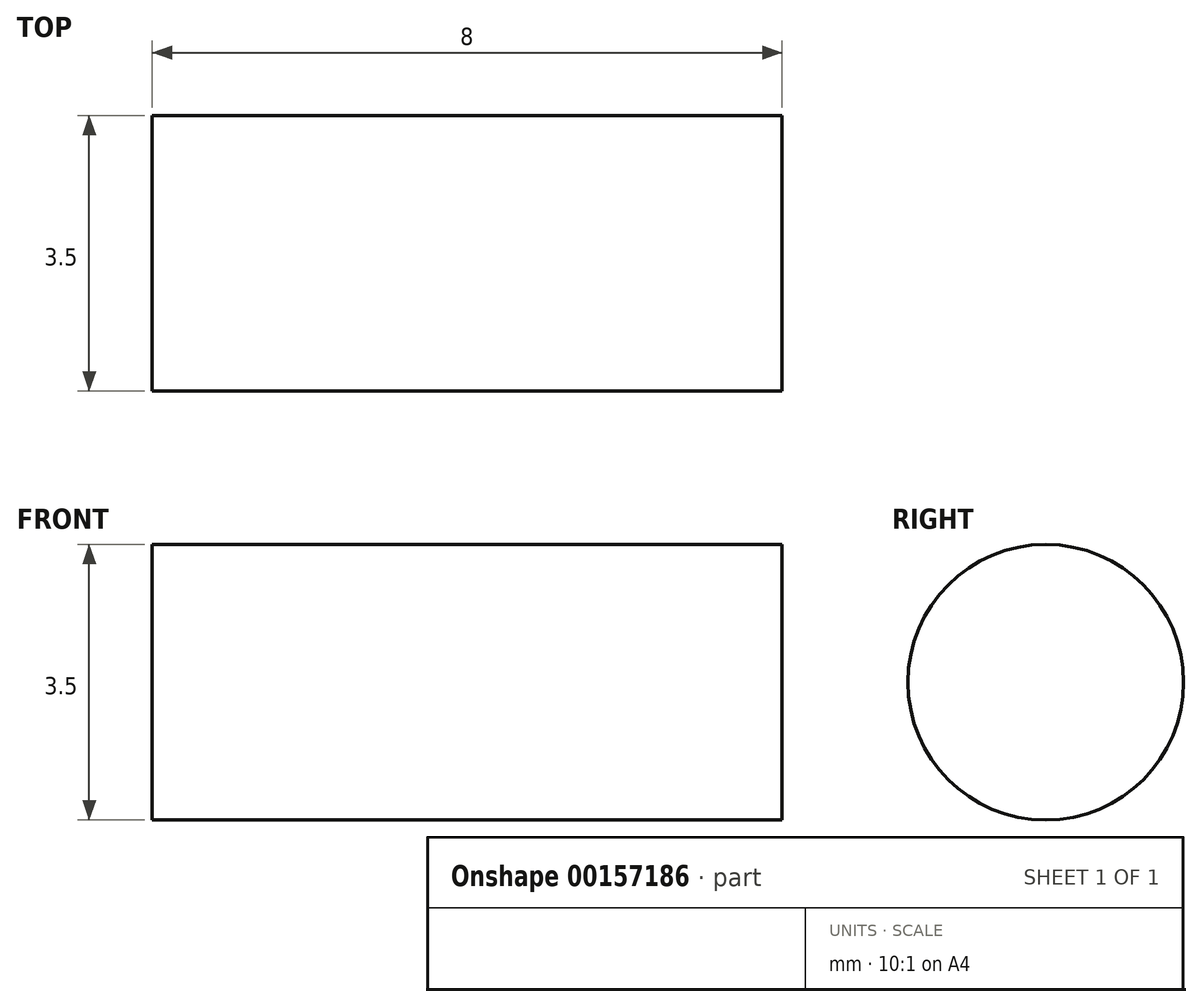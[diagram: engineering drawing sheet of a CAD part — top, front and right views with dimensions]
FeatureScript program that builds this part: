
annotation { "Feature Type Name" : "Feature", "Feature Type Description" : "" }
export const myFeature = defineFeature(function(context is Context, id is Id, definition is map)
    precondition{}
    {
        {
            var Q0;
            Q0=qCreatedBy(makeId("Right.planeOp"),FACE);
            var sketch = newSketch(context, id + "F0", { "sketchPlane" : qUnion([Q0])});
            skCircle(sketch, "E0", {"center": v(0, 0) * mm, "radius": 1.75 * mm});
            skSolve(sketch);
        }
        {
            var Q0;
            Q0 = qSketchRegion(id + "F0", true);
            extrude(context, id + "F1", {"entities" : qUnion([Q0]), "depth" : 8 * mm});
        }
    });
